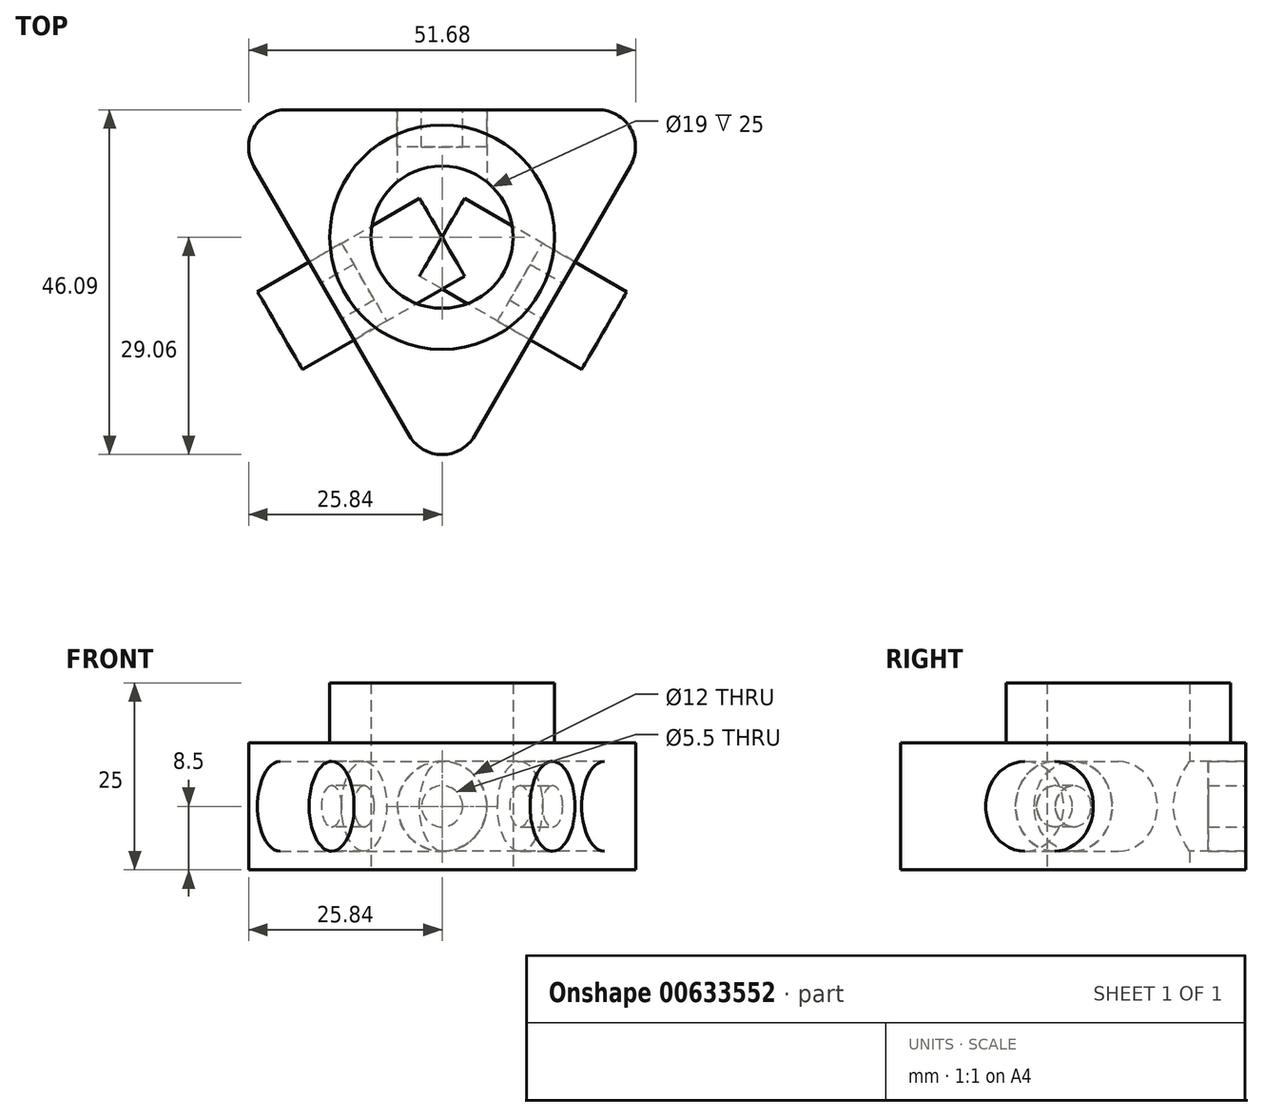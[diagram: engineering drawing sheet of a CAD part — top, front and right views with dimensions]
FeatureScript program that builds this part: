
annotation { "Feature Type Name" : "Feature", "Feature Type Description" : "" }
export const myFeature = defineFeature(function(context is Context, id is Id, definition is map)
    precondition{}
    {
        {
            var Q0;
            Q0=qCreatedBy(makeId("Top.planeOp"),FACE);
            var sketch = newSketch(context, id + "F0", { "sketchPlane" : qUnion([Q0])});
            skLineSegment(sketch, "E0", {"start": v(-29.5, 17.03) * mm, "end": v(29.5, 17.03) * mm, "construction": true});
            skLineSegment(sketch, "E1", {"start": v(25.17, 9.53) * mm, "end": v(4.33, -26.56) * mm});
            skLineSegment(sketch, "E2", {"start": v(-4.33, -26.56) * mm, "end": v(-25.17, 9.53) * mm});
            skCircle(sketch, "E3", {"center": v(0, 0) * mm, "radius": 34.06 * mm, "construction": true});
            skCircle(sketch, "E4", {"center": v(0, 0) * mm, "radius": 9.5 * mm});
            skLineSegment(sketch, "E5", {"start": v(0, 0) * mm, "end": v(29.5, 17.03) * mm, "construction": true});
            skLineSegment(sketch, "E6.MirrorCS", {"start": v(20.84, 17.03) * mm, "end": v(-20.84, 17.03) * mm});
            skPoint(sketch, "E7.visualSharp", {"position": v(-29.5, 17.03) * mm});
            skArc(sketch, "E7.filletArc", {"start": v(-20.84, 17.03) * mm, "mid": v(-25.17, 14.53) * mm, "end": v(-25.17, 9.53) * mm});
            skPoint(sketch, "E8.visualSharp", {"position": v(29.5, 17.03) * mm});
            skArc(sketch, "E8.filletArc", {"start": v(25.17, 9.53) * mm, "mid": v(25.17, 14.53) * mm, "end": v(20.84, 17.03) * mm});
            skPoint(sketch, "E9.visualSharp", {"position": v(0, -34.06) * mm});
            skArc(sketch, "E9.filletArc", {"start": v(-4.33, -26.56) * mm, "mid": v(0, -29.06) * mm, "end": v(4.33, -26.56) * mm});
            skLineSegment(sketch, "E10", {"start": v(-29.5, 17.03) * mm, "end": v(0, -34.06) * mm, "construction": true});
            skLineSegment(sketch, "E11", {"start": v(0, -34.06) * mm, "end": v(29.5, 17.03) * mm, "construction": true});
            skSolve(sketch);
        }
        {
            var Q0;
            Q0=makeQuery(id+"F0.imprint","IMPRINT",FACE,{"disambiguationData":[TD([[makeQuery(id+"F0.imprint","IMPRINT",EDGE,{"derivedFrom":sQuery(id+"F0.wireOp",EDGE,"E4")}),-1.0]])]});
            extrude(context, id + "F1", {"entities" : qUnion([Q0]), "endBound" : BoundingType.SYMMETRIC, "depth" : 17 * mm, "offsetDistance" : 25 * mm});
        }
        {
            var Q0;
            Q0=qCreatedBy(makeId("Front.planeOp"),FACE);
            var sketch = newSketch(context, id + "F2", { "sketchPlane" : qUnion([Q0])});
            skCircle(sketch, "E12", {"center": v(0, 0) * mm, "radius": 6 * mm});
            skSolve(sketch);
        }
        {
            var Q0;
            Q0=qSketchRegion(id+"F2",true);
            extrude(context, id + "F3", {"entities" : qUnion([Q0]), "oppositeDirection" : true, "depth" : 25 * mm, "offsetDistance" : 25 * mm});
        }
        {
            var Q0;
            Q0=makeQuery(id+"F3.opExtrude","SWEPT_BODY",BODY,{"disambiguationData":[OSD([sQuery(id+"F2.wireOp",EDGE,"E12")])]});
            var Q1;
            Q1=sQuery(id+"F0.wireOp",EDGE,"E4");
            circularPattern(context, id + "F4", {"entities" : qUnion([Q0]), "axis" : qUnion([Q1]), "angle" : 360 * degree, "instanceCount" : 3, "equalSpace" : true});
        }
        {
            var Q0;
            Q0=makeQuery(id+"F3.opExtrude","SWEPT_BODY",BODY,{"disambiguationData":[OSD([sQuery(id+"F2.wireOp",EDGE,"E12")])]});
            var Q1;
            Q1=makeQuery(id+"F1.opExtrude","SWEPT_BODY",BODY,{"disambiguationData":[OSD([sQuery(id+"F0.wireOp",EDGE,"8567cb31-eef4-4487-9e7d-64f7d120fd18.0"),sQuery(id+"F0.wireOp",EDGE,"8567cb31-eef4-4487-9e7d-64f7d120fd18.1"),sQuery(id+"F0.wireOp",EDGE,"8567cb31-eef4-4487-9e7d-64f7d120fd18.2"),sQuery(id+"F0.wireOp",EDGE,"99e7613c-3a71-48ef-a2ed-1ba2aef9368b.filletArc"),sQuery(id+"F0.wireOp",EDGE,"cfcb64ef-2180-43a3-8ec9-52d5588a1f2f.filletArc"),sQuery(id+"F0.wireOp",EDGE,"6011dbe8-f45c-4d00-b308-e3a8662c87ca.filletArc"),sQuery(id+"F0.wireOp",EDGE,"E4")])]});
            booleanBodies(context, id + "F5", {"operationType" : BooleanOperationType.SUBTRACTION, "tools" : qUnion([Q0]), "targets" : qUnion([Q1])});
        }
        {
            var Q0;
            Q0=makeQuery(id+"F1.opExtrude","SWEPT_FACE",FACE,{"disambiguationData":[OSD([sQuery(id+"F0.wireOp",EDGE,"E6.MirrorCS")])]});
            var sketch = newSketch(context, id + "F6", { "sketchPlane" : qUnion([Q0])});
            skCircle(sketch, "E13", {"center": v(0, 0) * mm, "radius": 6 * mm});
            skCircle(sketch, "E14", {"center": v(0, 0) * mm, "radius": 2.75 * mm});
            skSolve(sketch);
        }
        {
            var Q0;
            Q0=makeQuery(id+"F6.imprint","IMPRINT",FACE,{"disambiguationData":[TD([[makeQuery(id+"F6.imprint","IMPRINT",EDGE,{"derivedFrom":sQuery(id+"F6.wireOp",EDGE,"E13")}),-1.0]])]});
            extrude(context, id + "F7", {"entities" : qUnion([Q0]), "oppositeDirection" : true, "depth" : 5 * mm, "offsetDistance" : 25 * mm});
        }
        {
            var Q0;
            Q0=makeQuery(id+"F7.opExtrude","SWEPT_BODY",BODY,{"disambiguationData":[OSD([sQuery(id+"F6.wireOp",EDGE,"E13"),sQuery(id+"F6.wireOp",EDGE,"E14")])]});
            var Q1;
            Q1=makeQuery(id+"F1.opExtrude","CAP_EDGE",EDGE,{"disambiguationData":[OSD([sQuery(id+"F0.wireOp",EDGE,"E4")])],"isStart":false});
            circularPattern(context, id + "F8", {"entities" : qUnion([Q0]), "axis" : qUnion([Q1]), "angle" : 360 * degree, "instanceCount" : 3, "equalSpace" : true});
        }
        {
            var Q0;
            Q0=makeQuery(id+"F1.opExtrude","CAP_FACE",FACE,{"disambiguationData":[OSD([sQuery(id+"F0.wireOp",EDGE,"E1"),sQuery(id+"F0.wireOp",EDGE,"E2"),sQuery(id+"F0.wireOp",EDGE,"E4"),sQuery(id+"F0.wireOp",EDGE,"E6.MirrorCS"),sQuery(id+"F0.wireOp",EDGE,"E7.filletArc"),sQuery(id+"F0.wireOp",EDGE,"E8.filletArc"),sQuery(id+"F0.wireOp",EDGE,"E9.filletArc")])],"isStart":false});
            var sketch = newSketch(context, id + "F9", { "sketchPlane" : qUnion([Q0])});
            skCircle(sketch, "E15", {"center": v(0, 0) * mm, "radius": 15 * mm});
            skSolve(sketch);
        }
        {
            var Q0;
            Q0=makeQuery(id+"F9.imprint","IMPRINT",FACE,{"disambiguationData":[TD([[makeQuery(id+"F9.imprint","IMPRINT",EDGE,{"derivedFrom":sQuery(id+"F9.wireOp",EDGE,"E15")}),1.0]])]});
            extrude(context, id + "F10", {"entities" : qUnion([Q0]), "operationType" : NewBodyOperationType.ADD, "depth" : 8 * mm, "offsetDistance" : 25 * mm});
        }
    });
